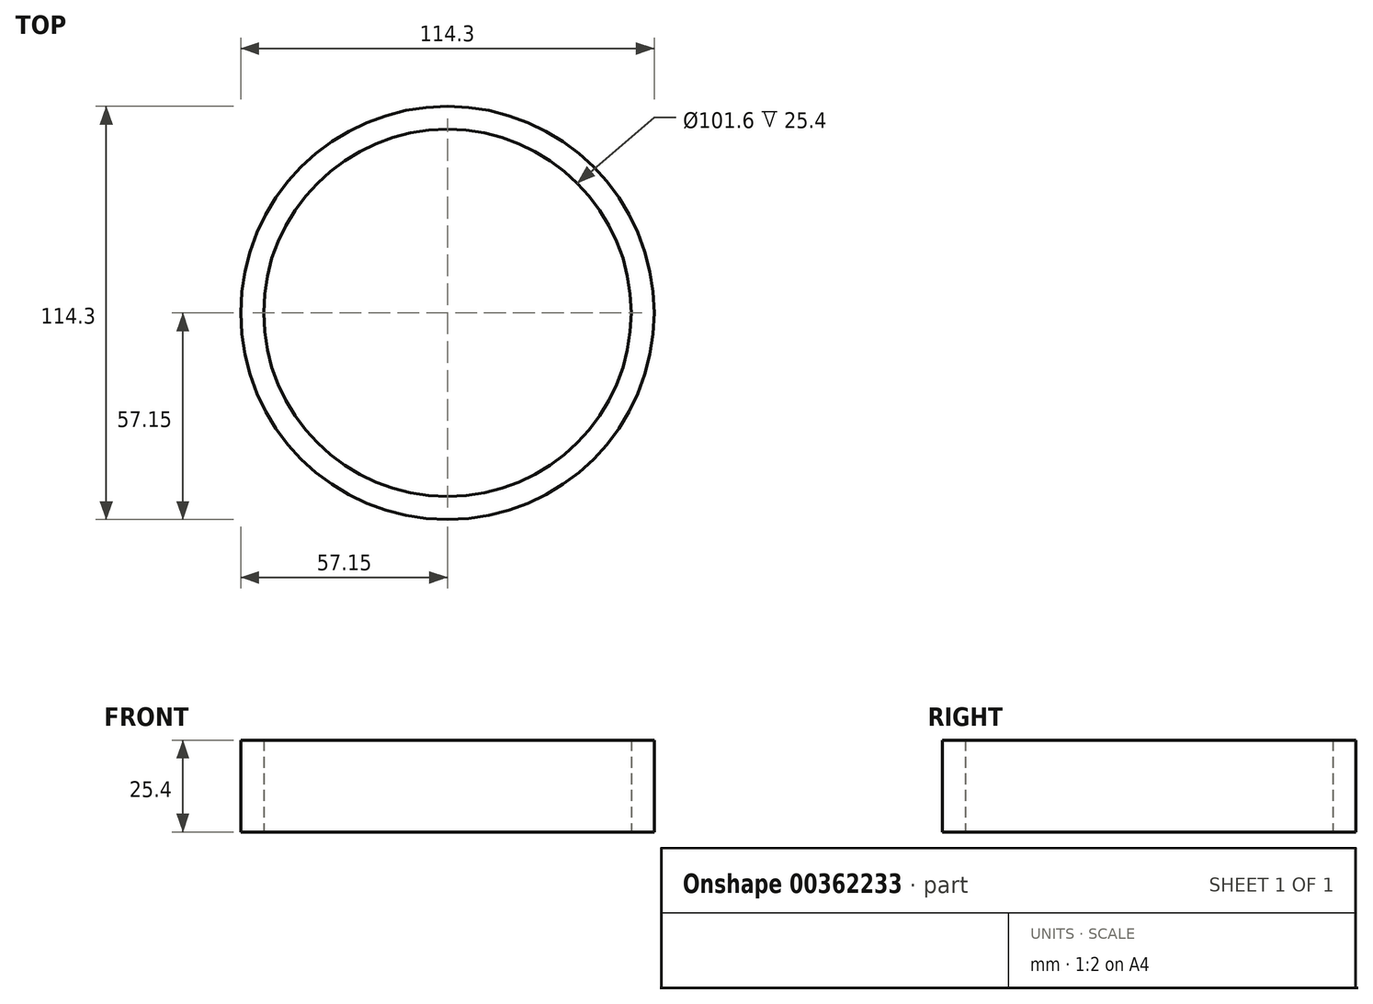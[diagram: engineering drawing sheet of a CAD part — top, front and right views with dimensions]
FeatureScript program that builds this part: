
annotation { "Feature Type Name" : "Feature", "Feature Type Description" : "" }
export const myFeature = defineFeature(function(context is Context, id is Id, definition is map)
    precondition{}
    {
        {
            var Q0;
            Q0=qCreatedBy(makeId("Top.planeOp"),FACE);
            var sketch = newSketch(context, id + "F0", { "sketchPlane" : qUnion([Q0])});
            skCircle(sketch, "E0", {"center": v(0, 0) * mm, "radius": 50.8 * mm});
            skCircle(sketch, "E1", {"center": v(0, 0) * mm, "radius": 57.15 * mm});
            skCircle(sketch, "E2.cCircle", {"center": v(0, 0) * mm, "radius": 57.15 * mm, "construction": true});
            skCircle(sketch, "E3.cCircle", {"center": v(0, 0) * mm, "radius": 50.8 * mm, "construction": true});
            skLineSegment(sketch, "E4", {"start": v(-48.31, 15.7) * mm, "end": v(29.86, -41.1) * mm});
            skLineSegment(sketch, "E5", {"start": v(48.31, 15.7) * mm, "end": v(-48.31, 15.7) * mm});
            skLineSegment(sketch, "E6", {"start": v(-54.35, 17.66) * mm, "end": v(54.35, 17.66) * mm});
            skLineSegment(sketch, "E7", {"start": v(54.35, 17.66) * mm, "end": v(-33.6, -46.24) * mm});
            skLineSegment(sketch, "E8", {"start": v(-29.86, -41.1) * mm, "end": v(48.31, 15.7) * mm});
            skLineSegment(sketch, "E9", {"start": v(0, 57.15) * mm, "end": v(-33.6, -46.24) * mm});
            skLineSegment(sketch, "E10", {"start": v(0, 57.15) * mm, "end": v(33.6, -46.24) * mm});
            skLineSegment(sketch, "E11", {"start": v(-54.35, 17.66) * mm, "end": v(33.6, -46.24) * mm});
            skLineSegment(sketch, "E12", {"start": v(-29.86, -41.1) * mm, "end": v(0, 50.8) * mm});
            skLineSegment(sketch, "E13", {"start": v(0, 50.8) * mm, "end": v(29.86, -41.1) * mm});
            skLineSegment(sketch, "E14", {"start": v(0, 57.15) * mm, "end": v(-49.5, -28.58) * mm});
            skLineSegment(sketch, "E15", {"start": v(-44, -25.4) * mm, "end": v(0, 50.8) * mm});
            skLineSegment(sketch, "E16", {"start": v(0, 50.8) * mm, "end": v(44, -25.4) * mm});
            skLineSegment(sketch, "E17", {"start": v(49.5, -28.57) * mm, "end": v(0, 57.15) * mm});
            skLineSegment(sketch, "E18", {"start": v(-49.5, -28.58) * mm, "end": v(49.5, -28.57) * mm});
            skLineSegment(sketch, "E19", {"start": v(44, -25.4) * mm, "end": v(-44, -25.4) * mm});
            skLineSegment(sketch, "E20", {"start": v(-44, 25.4) * mm, "end": v(0, -50.8) * mm});
            skLineSegment(sketch, "E21", {"start": v(-0.57, -50.45) * mm, "end": v(44, 25.4) * mm});
            skLineSegment(sketch, "E22", {"start": v(-44, 25.4) * mm, "end": v(44, 25.4) * mm});
            skLineSegment(sketch, "E23", {"start": v(-49.5, 28.57) * mm, "end": v(0, -57.15) * mm});
            skLineSegment(sketch, "E24", {"start": v(0, -57.15) * mm, "end": v(49.5, 28.58) * mm});
            skLineSegment(sketch, "E25", {"start": v(49.5, 28.58) * mm, "end": v(-49.5, 28.57) * mm});
            skSolve(sketch);
        }
        {
            var Q0;
            Q0 = qSketchRegion(id + "F0", true);
            var Q1;
            {var subQ0=sQuery(id+"F0.wireOp",EDGE,"E14");var subQ1=sQuery(id+"F0.wireOp",EDGE,"E0");var subQ2=makeQuery(id+"F0.imprint","INTERSECT",VERTEX,{"disambiguationData":[OD(0.0)],"derivedFrom":[subQ1,subQ0]});Q1=makeQuery(id+"F0.imprint","IMPRINT",FACE,{"disambiguationData":[TD([[makeQuery(id+"F0.imprint","IMPRINT",EDGE,{"disambiguationData":[TD([[subQ2,-1.0]])],"derivedFrom":subQ1}),-1.0]])]});}
            extrude(context, id + "F1", {"entities" : qUnion([Q0, Q1]), "depth" : 2.54 * mm});
        }
        {
            var Q0;
            Q0 = qSketchRegion(id + "F0", true);
            extrude(context, id + "F2", {"entities" : qUnion([Q0]), "operationType" : NewBodyOperationType.ADD, "depth" : 25.4 * mm});
        }
    });
